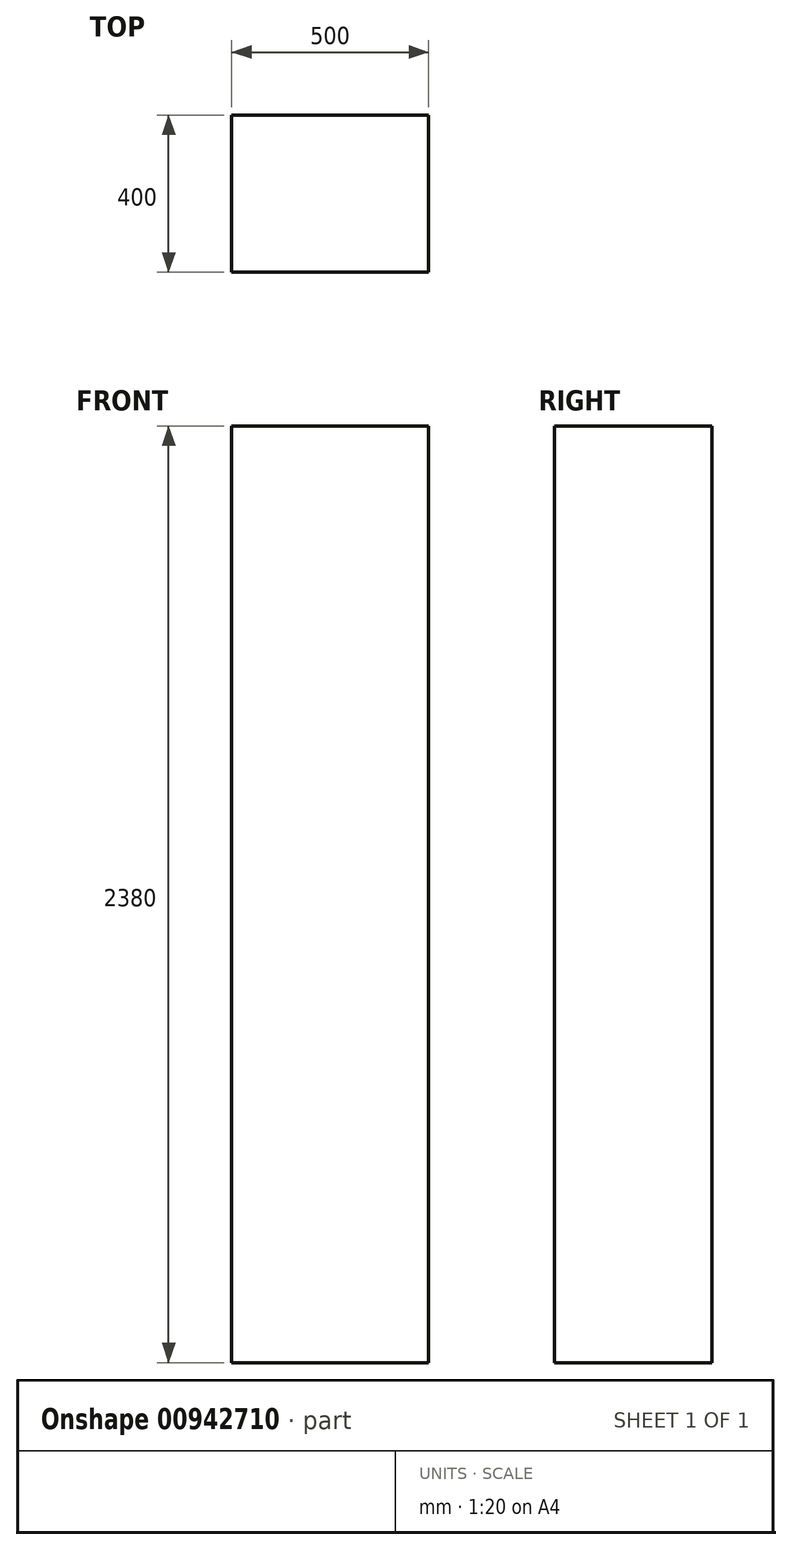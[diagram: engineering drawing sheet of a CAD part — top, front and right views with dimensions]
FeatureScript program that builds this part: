
annotation { "Feature Type Name" : "Feature", "Feature Type Description" : "" }
export const myFeature = defineFeature(function(context is Context, id is Id, definition is map)
    precondition{}
    {
        {
            var Q0;
            Q0=qCreatedBy(makeId("Top.planeOp"),FACE);
            var sketch = newSketch(context, id + "F0", { "sketchPlane" : qUnion([Q0])});
            skLineSegment(sketch, "E0.bottom", {"start": v(-250, 200) * mm, "end": v(250, 200) * mm});
            skLineSegment(sketch, "E0.top", {"start": v(-250, -200) * mm, "end": v(250, -200) * mm});
            skLineSegment(sketch, "E0.left", {"start": v(-250, -200) * mm, "end": v(-250, 200) * mm});
            skLineSegment(sketch, "E0.right", {"start": v(250, -200) * mm, "end": v(250, 200) * mm});
            skLineSegment(sketch, "E1", {"start": v(-250, 0) * mm, "end": v(0, 0) * mm, "construction": true});
            skLineSegment(sketch, "E2", {"start": v(0, 0) * mm, "end": v(250, 0) * mm, "construction": true});
            skLineSegment(sketch, "E3", {"start": v(0, 200) * mm, "end": v(0, 0) * mm, "construction": true});
            skPoint(sketch, "E3.endSnap0", {"position": v(0, 200) * mm});
            skLineSegment(sketch, "E4", {"start": v(0, 0) * mm, "end": v(0, -200) * mm, "construction": true});
            skSolve(sketch);
        }
        {
            var Q0;
            Q0 = qSketchRegion(id + "F0", true);
            var Q1;
            Q1=makeQuery(id+"F0.imprint","IMPRINT",FACE,{"disambiguationData":[TD([[makeQuery(id+"F0.imprint","IMPRINT",EDGE,{"derivedFrom":sQuery(id+"F0.wireOp",EDGE,"E0.bottom")}),-1.0]])]});
            extrude(context, id + "F1", {"entities" : qUnion([Q0, Q1]), "depth" : 2380 * mm, "offsetDistance" : 25 * mm});
        }
    });
